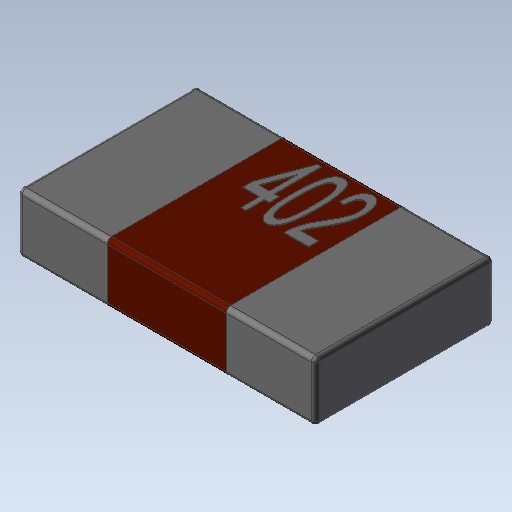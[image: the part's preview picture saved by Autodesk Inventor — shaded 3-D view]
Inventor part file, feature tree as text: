
AUTODESK INVENTOR PART (.ipt)
format: ipt  version: 2020 (Build 240168000, 168)  size: 193,536 bytes
history: native  units: in
note: dims shown in document units (in); Inventor stores cm internally (conversion verified against a paired STEP export)
features: extrude x1
ambient origin geometry x8: Origin, YZ Plane, XZ Plane, XY Plane, X Axis, Y Axis, Z Axis, Center Point
bodies: Solid1 (feature_tree)
feature tree (1):
  extrude  "Extrude2"  [1 undecoded]
note: 1 required parameter value undecoded (feature->parameter linkage not recoverable at this tier; creation-order binding heuristic only, values carry confidence <= 0.55)
